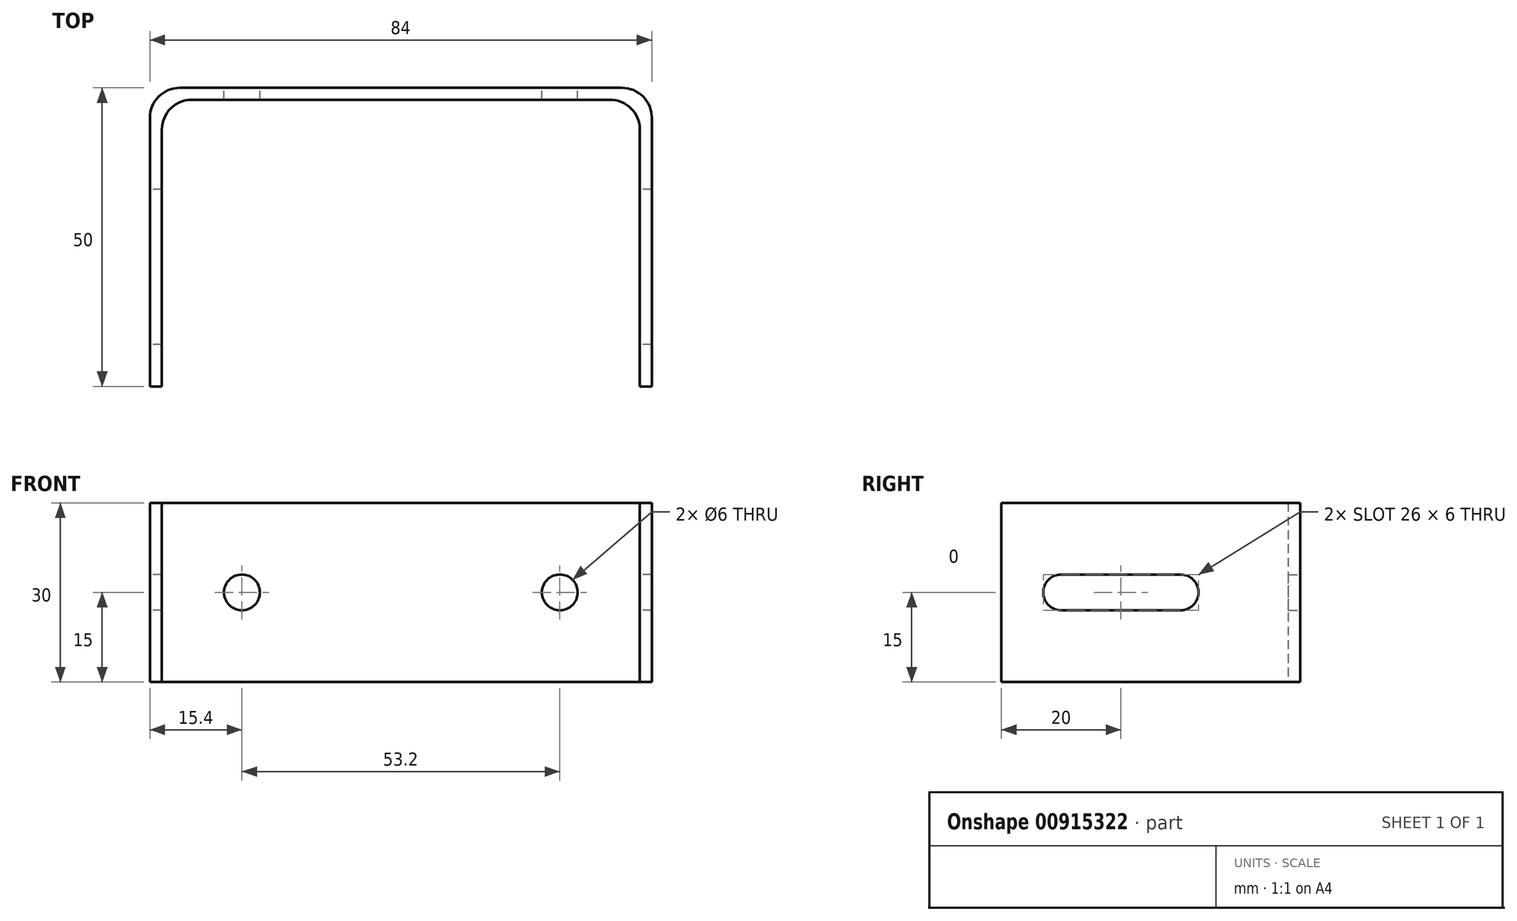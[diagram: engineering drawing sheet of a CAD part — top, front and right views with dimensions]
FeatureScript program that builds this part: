
annotation { "Feature Type Name" : "Feature", "Feature Type Description" : "" }
export const myFeature = defineFeature(function(context is Context, id is Id, definition is map)
    precondition{}
    {
        {
            var Q0;
            Q0=qCreatedBy(makeId("Top.planeOp"),FACE);
            var sketch = newSketch(context, id + "F0", { "sketchPlane" : qUnion([Q0])});
            skLineSegment(sketch, "E0.bottom", {"start": v(0, 0) * mm, "end": v(2, 0) * mm});
            skLineSegment(sketch, "E0.top", {"start": v(5, 50) * mm, "end": v(79, 50) * mm});
            skLineSegment(sketch, "E0.left", {"start": v(0, 0) * mm, "end": v(0, 45) * mm});
            skLineSegment(sketch, "E0.right", {"start": v(84, 0) * mm, "end": v(84, 45) * mm});
            skLineSegment(sketch, "E1.top", {"start": v(7, 48) * mm, "end": v(77, 48) * mm});
            skLineSegment(sketch, "E1.left", {"start": v(2, 0) * mm, "end": v(2, 43) * mm});
            skLineSegment(sketch, "E1.right", {"start": v(82, 0) * mm, "end": v(82, 43) * mm});
            skLineSegment(sketch, "E2.trimOffspring", {"start": v(82, 0) * mm, "end": v(84, 0) * mm});
            skPoint(sketch, "E3.visualSharp", {"position": v(0, 50) * mm});
            skArc(sketch, "E3.filletArc", {"start": v(5, 50) * mm, "mid": v(1.46, 48.54) * mm, "end": v(0, 45) * mm});
            skPoint(sketch, "E4.visualSharp", {"position": v(2, 48) * mm});
            skArc(sketch, "E4.filletArc", {"start": v(7, 48) * mm, "mid": v(3.46, 46.54) * mm, "end": v(2, 43) * mm});
            skPoint(sketch, "E5.visualSharp", {"position": v(82, 48) * mm});
            skArc(sketch, "E5.filletArc", {"start": v(82, 43) * mm, "mid": v(80.54, 46.54) * mm, "end": v(77, 48) * mm});
            skPoint(sketch, "E6.visualSharp", {"position": v(84, 50) * mm});
            skArc(sketch, "E6.filletArc", {"start": v(84, 45) * mm, "mid": v(82.54, 48.54) * mm, "end": v(79, 50) * mm});
            skSolve(sketch);
        }
        {
            var Q0;
            Q0 = qSketchRegion(id + "F0", true);
            extrude(context, id + "F1", {"entities" : qUnion([Q0]), "depth" : 30 * mm, "offsetDistance" : 25 * mm});
        }
        {
            var Q0;
            Q0=makeQuery(id+"F1.opExtrude","SWEPT_FACE",FACE,{"disambiguationData":[OSD([sQuery(id+"F0.wireOp",EDGE,"E0.left")])]});
            var sketch = newSketch(context, id + "F2", { "sketchPlane" : qUnion([Q0])});
            skArc(sketch, "E7", {"start": v(-30, 18) * mm, "mid": v(-33, 15) * mm, "end": v(-30, 12) * mm});
            skArc(sketch, "E8", {"start": v(-10, 12) * mm, "mid": v(-7, 15) * mm, "end": v(-10, 18) * mm});
            skLineSegment(sketch, "E9", {"start": v(-30, 18) * mm, "end": v(-10, 18) * mm});
            skLineSegment(sketch, "E10", {"start": v(-30, 12) * mm, "end": v(-10, 12) * mm});
            skSolve(sketch);
        }
        {
            var Q0;
            Q0=makeQuery(id+"F2.imprint","IMPRINT",FACE,{"disambiguationData":[TD([[makeQuery(id+"F2.imprint","IMPRINT",EDGE,{"derivedFrom":sQuery(id+"F2.wireOp",EDGE,"E7")}),1.0]])]});
            extrude(context, id + "F3", {"entities" : qUnion([Q0]), "operationType" : NewBodyOperationType.REMOVE, "endBound" : BoundingType.THROUGH_ALL, "oppositeDirection" : true, "depth" : 25 * mm, "offsetDistance" : 25 * mm});
        }
        {
            var Q0;
            Q0=makeQuery(id+"F1.opExtrude","SWEPT_FACE",FACE,{"disambiguationData":[OSD([sQuery(id+"F0.wireOp",EDGE,"E0.top")])]});
            var sketch = newSketch(context, id + "F4", { "sketchPlane" : qUnion([Q0])});
            skCircle(sketch, "E11", {"center": v(-68.6, 15) * mm, "radius": 3 * mm});
            skCircle(sketch, "E12", {"center": v(-15.4, 15) * mm, "radius": 3 * mm});
            skLineSegment(sketch, "E13", {"start": v(-42, 30) * mm, "end": v(-42, 0) * mm, "construction": true});
            skSolve(sketch);
        }
        {
            var Q0;
            Q0 = qSketchRegion(id + "F4", true);
            extrude(context, id + "F5", {"entities" : qUnion([Q0]), "operationType" : NewBodyOperationType.REMOVE, "endBound" : BoundingType.THROUGH_ALL, "oppositeDirection" : true, "depth" : 25 * mm, "offsetDistance" : 25 * mm});
        }
    });
